# Revit family: DRF367500AP
name_source: partatom
category: Specialty Equipment
revit_build: Autodesk Revit MEP 2014 (Build: 20130308_1515(x64)
units: mm (PartAtom-declared; Revit-internal decimal feet)

## types (1)
- DRF367500AP
    Adjustable Shelves - Refrigerator = 2 ea
    Annual Energy Consumption = 549 kWh/year
    Crisper Drawers = 2 ea
    Current (A) = 6.0
    Defrost Process - Freezer = Yes
    Deodorizing Filter = Yes
    Depth = 25"
    Description = 36-INCH FRENCH DOOR BOTTOM FREEZER
    Door = Stainless Steel
    Door Bins -Refrigerator = 6 ea
    Door Open Alarm = Yes
    Double Cooling (2 evaporators, 1 compressor) = Yes
    ENERGY STAR® Qualified = Yes
    Feezer = 5°(-15°) to -8° (-23°)
    Feezer - Power Freeze = -8°(-23°)
    Freezer Drawers = 2 ea
    Freezer Gross Capacity (cu.ft.) = 6.8 cu. ft.
    Frequency (Hz) = 60
    FreshZone™ Drawer = Yes - Cheese (37°) / Cold Drinks (33°) / Meat (29°)
    Full Extension Drawers at 90º Door Opening Angle = Yes
    Full Width Shelves - Refrigerator = 2 ea
    Handle = Stainless Steel
    Height = 83 3/8"
    Icemaker = Dual Icemaker for Standard and Cocktail Ice™
    Interior Material = SteelCool™ Stainless Steel Interior
    Internal Water Dispenser = Yes
    Lighting = 3DLighting™
    Manufacturer = Dacor
    Model = DRF367500AP
    Panel Ready = Yes
    Plug Type = 120 V, 3 Prong
    Power Cool - Refrigerator = Yes
    Power Cord Length (in.) = 78 3/4
    Precise Cooling = Frost-Free
    Push-To-Open™ Door Assist = No
    Refrigerator = 34°(1°) to 44°(7°)
    Refrigerator - Power Cool = 34°(1°)
    Refrigerator Gross Capacity (cu.ft.) = 14.5 cu. ft.
    Shelf Material - Refrigerator = Tempered Glass Shelves w/Metal Trim
    Special Modes = Sabbath Mode
    Support = Plastic-Black
    Total Unit Gross Capacity (cu.ft.) - AHAM = 21.3 cu. ft.
    Unit = Stainless Steel
    Volts (V) = 115
    Width = 35 3/4"
    iQ RemoteView™ Camera = No

## geometry (parser evidence)
native form markers: Sweep x1
no freeform markers — native parametric forms only
